# Revit family: Haworth_Enclose_Accessories_WallStartCompressible
name_source: partatom
category: Furniture Systems
revit_build: Autodesk Revit 2018 (Build: 20170223_1515(x64)
units: mm (PartAtom-declared; Revit-internal decimal feet)

## family parameters
Always vertical = Yes
Cut with Voids When Loaded = No
OmniClass Number = 23.25.40.14
OmniClass Title = Demountable Partitions
Part Type = Normal
Room Calculation Point = No
Round Connector Dimension = Use Diameter
Shared = No
Work Plane-Based = No

## types (1)
- Adjustable
    Actual Height = 108 "
    Assembly Code = C1010200
    Depth = 3.61 "
    Description = Wall Start Compressible
    Height = 108 "
    Manufacturer = Haworth
    Material Options = http://surfaces.haworth.com
    Max. Height = 144 "
    Min. Height = 24 "
    Min/ Max Height = 24-144 in.
    Model = Haworth - Enclose Accessories
    Revision Number = 2
    Sustainability Info = http://www.haworth.com
    URL = www.haworth.com
    URL - Product = http://www.haworth.com
    Warranty = http://www.haworth.com
    Width = 0.4198 "

## geometry (parser evidence)
native form markers: Sweep x3
no freeform markers — native parametric forms only
